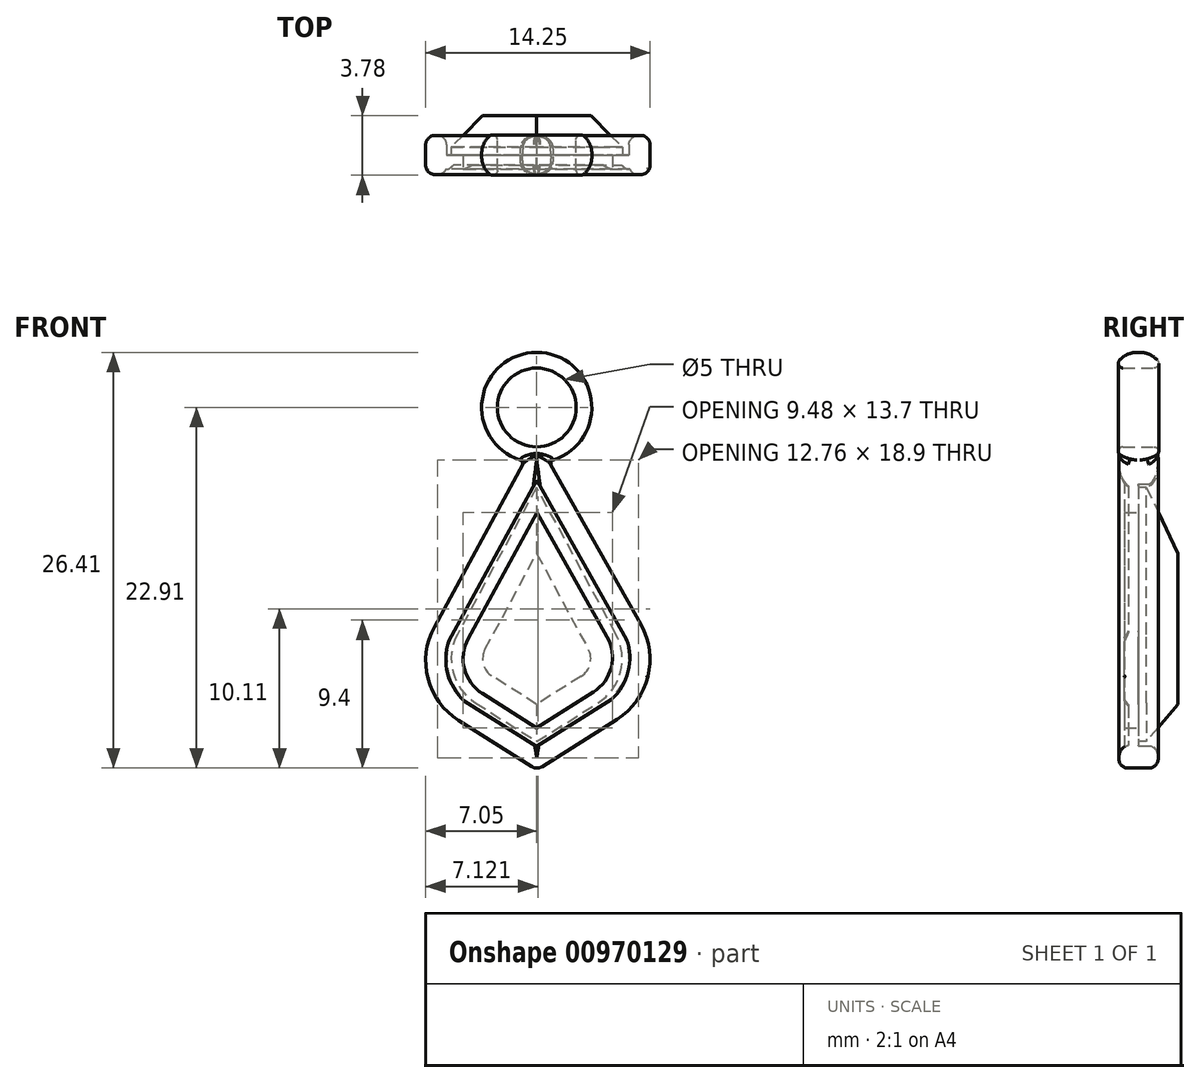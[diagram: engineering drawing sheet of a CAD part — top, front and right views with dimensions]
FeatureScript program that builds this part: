
annotation { "Feature Type Name" : "Feature", "Feature Type Description" : "" }
export const myFeature = defineFeature(function(context is Context, id is Id, definition is map)
    precondition{}
    {
        {
            var Q0;
            Q0=qCreatedBy(makeId("Front.planeOp"),FACE);
            var sketch = newSketch(context, id + "F0", { "sketchPlane" : qUnion([Q0])});
            skCircle(sketch, "E0", {"center": v(0, 12.12) * mm, "radius": 3.5 * mm});
            skCircle(sketch, "E1", {"center": v(0, 12.12) * mm, "radius": 2.5 * mm});
            skSolve(sketch);
        }
        {
            var Q0;
            Q0=makeQuery(id+"F0.imprint","IMPRINT",FACE,{"disambiguationData":[TD([[makeQuery(id+"F0.imprint","IMPRINT",EDGE,{"derivedFrom":sQuery(id+"F0.wireOp",EDGE,"E0")}),1.0]])]});
            extrude(context, id + "F1", {"entities" : qUnion([Q0]), "depth" : 1.5 * mm, "offsetDistance" : 25 * mm, "hasSecondDirection" : true, "secondDirectionOppositeDirection" : true, "secondDirectionDepth" : 1.5 * mm});
        }
        {
            var Q0;
            Q0=makeQuery(id+"F1.opExtrude","CAP_EDGE",EDGE,{"disambiguationData":[OSD([sQuery(id+"F0.wireOp",EDGE,"E0")])],"isStart":true});
            var Q1;
            Q1=makeQuery(id+"F1.opExtrude","CAP_EDGE",EDGE,{"disambiguationData":[OSD([sQuery(id+"F0.wireOp",EDGE,"E0")])],"isStart":false});
            fillet(context, id + "F2", {"entities" : qUnion([Q0, Q1]), "radius" : 1.5 * mm, "tangentPropagation" : true, "allowEdgeOverflow" : false});
        }
        {
            var Q0;
            Q0=makeQuery(id+"F1.opExtrude","SWEPT_FACE",FACE,{"disambiguationData":[OSD([sQuery(id+"F0.wireOp",EDGE,"E1")])]});
            var Q1;
            Q1=makeQuery(id+"F2.opFillet","BLEND_EDGE",EDGE,{"blendedFrom":[makeQuery(id+"F1.opExtrude","CAP_EDGE",EDGE,{"disambiguationData":[OSD([sQuery(id+"F0.wireOp",EDGE,"E0")])],"isStart":true}),makeQuery(id+"F1.opExtrude","SWEPT_FACE",FACE,{"disambiguationData":[OSD([sQuery(id+"F0.wireOp",EDGE,"E1")])]})],"blendedInto":[makeQuery(id+"F1.opExtrude","SWEPT_FACE",FACE,{"disambiguationData":[OSD([sQuery(id+"F0.wireOp",EDGE,"E1")])]})]});
            var Q2;
            Q2=makeQuery(id+"F2.opFillet","BLEND_EDGE",EDGE,{"blendedFrom":[makeQuery(id+"F1.opExtrude","CAP_EDGE",EDGE,{"disambiguationData":[OSD([sQuery(id+"F0.wireOp",EDGE,"E0")])],"isStart":false}),makeQuery(id+"F1.opExtrude","SWEPT_FACE",FACE,{"disambiguationData":[OSD([sQuery(id+"F0.wireOp",EDGE,"E1")])]})],"blendedInto":[makeQuery(id+"F1.opExtrude","SWEPT_FACE",FACE,{"disambiguationData":[OSD([sQuery(id+"F0.wireOp",EDGE,"E1")])]})]});
            fillet(context, id + "F3", {"entities" : qUnion([Q0, Q1, Q2]), "radius" : .3 * mm, "tangentPropagation" : true, "allowEdgeOverflow" : false});
        }
        {
            var Q0;
            Q0=qCreatedBy(makeId("Front.planeOp"),FACE);
            var sketch = newSketch(context, id + "F4", { "sketchPlane" : qUnion([Q0])});
            skLineSegment(sketch, "E2", {"start": v(-0.04, 10.14) * mm, "end": v(8.72, -5.4) * mm});
            skLineSegment(sketch, "E3", {"start": v(8.72, -5.4) * mm, "end": v(0, -10.9) * mm});
            skLineSegment(sketch, "E4.MirrorCS", {"start": v(0, 10.14) * mm, "end": v(-8.52, -5.52) * mm});
            skLineSegment(sketch, "E5.MirrorCS", {"start": v(-8.52, -5.52) * mm, "end": v(0, -10.9) * mm});
            skLineSegment(sketch, "E6.0", {"start": v(0, 7.53) * mm, "end": v(7.04, -4.97) * mm});
            skLineSegment(sketch, "E6.1", {"start": v(0, 7.53) * mm, "end": v(-6.86, -5.09) * mm});
            skLineSegment(sketch, "E6.2", {"start": v(-6.86, -5.09) * mm, "end": v(0, -9.42) * mm});
            skLineSegment(sketch, "E6.3", {"start": v(7.04, -4.97) * mm, "end": v(0, -9.42) * mm});
            skLineSegment(sketch, "E7.0", {"start": v(0.02, 5.46) * mm, "end": v(-5.53, -4.74) * mm});
            skLineSegment(sketch, "E7.1", {"start": v(0.02, 5.46) * mm, "end": v(5.7, -4.63) * mm});
            skLineSegment(sketch, "E7.2", {"start": v(5.7, -4.63) * mm, "end": v(0, -8.24) * mm});
            skLineSegment(sketch, "E7.3", {"start": v(-5.53, -4.74) * mm, "end": v(0, -8.24) * mm});
            skSolve(sketch);
        }
        {
            var Q0;
            Q0=makeQuery(id+"F4.imprint","IMPRINT",FACE,{"disambiguationData":[TD([[makeQuery(id+"F4.imprint","IMPRINT",EDGE,{"derivedFrom":sQuery(id+"F4.wireOp",EDGE,"E2")}),-1.0]])]});
            extrude(context, id + "F5", {"entities" : qUnion([Q0]), "depth" : 1.25 * mm, "offsetDistance" : 25 * mm, "hasSecondDirection" : true, "secondDirectionOppositeDirection" : true, "secondDirectionDepth" : 1.25 * mm});
        }
        {
            var Q0;
            Q0=makeQuery(id+"F5.opExtrude","SWEPT_EDGE",EDGE,{"disambiguationData":[OSD([sQuery(id+"F4.wireOp",EDGE,"E4.MirrorCS"),sQuery(id+"F4.wireOp",EDGE,"E5.MirrorCS")])]});
            var Q1;
            Q1=makeQuery(id+"F5.opExtrude","SWEPT_EDGE",EDGE,{"disambiguationData":[OSD([sQuery(id+"F4.wireOp",EDGE,"E2"),sQuery(id+"F4.wireOp",EDGE,"E3")])]});
            fillet(context, id + "F6", {"entities" : qUnion([Q0, Q1]), "radius" : 4.5 * mm, "tangentPropagation" : true, "allowEdgeOverflow" : false});
        }
        {
            var Q0;
            Q0=makeQuery(id+"F5.opExtrude","SWEPT_EDGE",EDGE,{"disambiguationData":[OSD([sQuery(id+"F4.wireOp",EDGE,"E6.0"),sQuery(id+"F4.wireOp",EDGE,"E6.3")])]});
            var Q1;
            Q1=makeQuery(id+"F5.opExtrude","SWEPT_EDGE",EDGE,{"disambiguationData":[OSD([sQuery(id+"F4.wireOp",EDGE,"E6.1"),sQuery(id+"F4.wireOp",EDGE,"E6.2")])]});
            fillet(context, id + "F7", {"entities" : qUnion([Q0, Q1]), "radius" : 3.5 * mm, "tangentPropagation" : true, "allowEdgeOverflow" : false});
        }
        {
            var Q0;
            {var subQ0=sQuery(id+"F4.wireOp",EDGE,"E3");var subQ1=sQuery(id+"F4.wireOp",EDGE,"E2");Q0=makeQuery(id+"F6.opFillet","BLEND_EDGE",EDGE,{"blendedFrom":[makeQuery(id+"F5.opExtrude","SWEPT_EDGE",EDGE,{"disambiguationData":[OSD([subQ1,subQ0])]}),makeQuery(id+"F5.opExtrude","CAP_FACE",FACE,{"disambiguationData":[OSD([subQ1,subQ0,sQuery(id+"F4.wireOp",EDGE,"E4.MirrorCS"),sQuery(id+"F4.wireOp",EDGE,"E5.MirrorCS"),sQuery(id+"F4.wireOp",EDGE,"E6.0"),sQuery(id+"F4.wireOp",EDGE,"E6.1"),sQuery(id+"F4.wireOp",EDGE,"E6.2"),sQuery(id+"F4.wireOp",EDGE,"E6.3")])],"isStart":false})],"blendedInto":[makeQuery(id+"F5.opExtrude","CAP_FACE",FACE,{"disambiguationData":[OSD([subQ1,subQ0,sQuery(id+"F4.wireOp",EDGE,"E4.MirrorCS"),sQuery(id+"F4.wireOp",EDGE,"E5.MirrorCS"),sQuery(id+"F4.wireOp",EDGE,"E6.0"),sQuery(id+"F4.wireOp",EDGE,"E6.1"),sQuery(id+"F4.wireOp",EDGE,"E6.2"),sQuery(id+"F4.wireOp",EDGE,"E6.3")])],"isStart":false})]});}
            var Q1;
            Q1=makeQuery(id+"F5.opExtrude","CAP_EDGE",EDGE,{"disambiguationData":[OSD([sQuery(id+"F4.wireOp",EDGE,"E3")])],"isStart":false});
            var Q2;
            Q2=makeQuery(id+"F5.opExtrude","CAP_EDGE",EDGE,{"disambiguationData":[OSD([sQuery(id+"F4.wireOp",EDGE,"E6.0")])],"isStart":false});
            var Q3;
            Q3=makeQuery(id+"F5.opExtrude","CAP_EDGE",EDGE,{"disambiguationData":[OSD([sQuery(id+"F4.wireOp",EDGE,"E5.MirrorCS")])],"isStart":false});
            var Q4;
            Q4=makeQuery(id+"F5.opExtrude","CAP_EDGE",EDGE,{"disambiguationData":[OSD([sQuery(id+"F4.wireOp",EDGE,"E6.2")])],"isStart":false});
            var Q5;
            {var subQ0=sQuery(id+"F4.wireOp",EDGE,"E5.MirrorCS");var subQ1=sQuery(id+"F4.wireOp",EDGE,"E4.MirrorCS");Q5=makeQuery(id+"F6.opFillet","BLEND_EDGE",EDGE,{"blendedFrom":[makeQuery(id+"F5.opExtrude","SWEPT_EDGE",EDGE,{"disambiguationData":[OSD([subQ1,subQ0])]}),makeQuery(id+"F5.opExtrude","CAP_FACE",FACE,{"disambiguationData":[OSD([sQuery(id+"F4.wireOp",EDGE,"E2"),sQuery(id+"F4.wireOp",EDGE,"E3"),subQ1,subQ0,sQuery(id+"F4.wireOp",EDGE,"E6.0"),sQuery(id+"F4.wireOp",EDGE,"E6.1"),sQuery(id+"F4.wireOp",EDGE,"E6.2"),sQuery(id+"F4.wireOp",EDGE,"E6.3")])],"isStart":true})],"blendedInto":[makeQuery(id+"F5.opExtrude","CAP_FACE",FACE,{"disambiguationData":[OSD([sQuery(id+"F4.wireOp",EDGE,"E2"),sQuery(id+"F4.wireOp",EDGE,"E3"),subQ1,subQ0,sQuery(id+"F4.wireOp",EDGE,"E6.0"),sQuery(id+"F4.wireOp",EDGE,"E6.1"),sQuery(id+"F4.wireOp",EDGE,"E6.2"),sQuery(id+"F4.wireOp",EDGE,"E6.3")])],"isStart":true})]});}
            var Q6;
            Q6=makeQuery(id+"F5.opExtrude","CAP_EDGE",EDGE,{"disambiguationData":[OSD([sQuery(id+"F4.wireOp",EDGE,"E6.1")])],"isStart":true});
            var Q7;
            Q7=makeQuery(id+"F5.opExtrude","CAP_EDGE",EDGE,{"disambiguationData":[OSD([sQuery(id+"F4.wireOp",EDGE,"E6.0")])],"isStart":true});
            var Q8;
            Q8=makeQuery(id+"F5.opExtrude","CAP_EDGE",EDGE,{"disambiguationData":[OSD([sQuery(id+"F4.wireOp",EDGE,"E3")])],"isStart":true});
            var Q9;
            Q9=makeQuery(id+"F5.opExtrude","SWEPT_EDGE",EDGE,{"disambiguationData":[OSD([sQuery(id+"F4.wireOp",EDGE,"E3"),sQuery(id+"F4.wireOp",EDGE,"E5.MirrorCS")])]});
            fillet(context, id + "F8", {"entities" : qUnion([Q0, Q1, Q2, Q3, Q4, Q5, Q6, Q7, Q8, Q9]), "radius" : .6 * mm, "tangentPropagation" : true, "allowEdgeOverflow" : false});
        }
        {
            var Q0;
            Q0=makeQuery(id+"F8.opFillet","BLEND_EDGE",EDGE,{"blendedFrom":[makeQuery(id+"F5.opExtrude","CAP_EDGE",EDGE,{"disambiguationData":[OSD([sQuery(id+"F4.wireOp",EDGE,"E6.0")])],"isStart":false}),makeQuery(id+"F5.opExtrude","CAP_EDGE",EDGE,{"disambiguationData":[OSD([sQuery(id+"F4.wireOp",EDGE,"E6.1")])],"isStart":false})],"blendedInto":[]});
            var Q1;
            Q1=makeQuery(id+"F5.opExtrude","SWEPT_EDGE",EDGE,{"disambiguationData":[OSD([sQuery(id+"F4.wireOp",EDGE,"E6.2"),sQuery(id+"F4.wireOp",EDGE,"E6.3")])]});
            fillet(context, id + "F9", {"entities" : qUnion([Q0, Q1]), "radius" : .25 * mm, "tangentPropagation" : true, "allowEdgeOverflow" : false});
        }
        {
            var Q0;
            Q0=makeQuery(id+"F5.opExtrude","SWEPT_EDGE",EDGE,{"disambiguationData":[OSD([sQuery(id+"F4.wireOp",EDGE,"E2"),sQuery(id+"F4.wireOp",EDGE,"E4.MirrorCS")])]});
            fillet(context, id + "F10", {"entities" : qUnion([Q0]), "radius" : .5 * mm, "tangentPropagation" : true, "allowEdgeOverflow" : false});
        }
        {
            var Q0;
            Q0=makeQuery(id+"F4.imprint","IMPRINT",FACE,{"disambiguationData":[TD([[makeQuery(id+"F4.imprint","IMPRINT",EDGE,{"derivedFrom":sQuery(id+"F4.wireOp",EDGE,"E6.0")}),-1.0]])]});
            extrude(context, id + "F11", {"entities" : qUnion([Q0]), "depth" : .9 * mm, "offsetDistance" : 25 * mm});
        }
        {
            var Q0;
            Q0=qCreatedBy(makeId("Front.planeOp"),FACE);
            var sketch = newSketch(context, id + "F12", { "sketchPlane" : qUnion([Q0])});
            skLineSegment(sketch, "E8", {"start": v(0, 7.05) * mm, "end": v(-6.5, -5) * mm});
            skLineSegment(sketch, "E9", {"start": v(-6.5, -5) * mm, "end": v(0, -9.1) * mm});
            skLineSegment(sketch, "E10.MirrorCS", {"start": v(6.5, -5) * mm, "end": v(0, -9.1) * mm});
            skLineSegment(sketch, "E11.MirrorCS", {"start": v(0, 7.05) * mm, "end": v(6.5, -5) * mm});
            skSolve(sketch);
        }
        {
            var Q0;
            Q0=qSketchRegion(id+"F12",true);
            extrude(context, id + "F13", {"entities" : qUnion([Q0]), "oppositeDirection" : true, "depth" : 2.5 * mm, "offsetDistance" : 25 * mm});
        }
        {
            var Q0;
            Q0=makeQuery(id+"F13.opExtrude","SWEPT_EDGE",EDGE,{"disambiguationData":[OSD([sQuery(id+"F12.wireOp",EDGE,"E8"),sQuery(id+"F12.wireOp",EDGE,"E9")])]});
            var Q1;
            Q1=makeQuery(id+"F13.opExtrude","SWEPT_EDGE",EDGE,{"disambiguationData":[OSD([sQuery(id+"F12.wireOp",EDGE,"E10.MirrorCS"),sQuery(id+"F12.wireOp",EDGE,"E11.MirrorCS")])]});
            fillet(context, id + "F14", {"entities" : qUnion([Q0, Q1]), "radius" : 3.3 * mm, "tangentPropagation" : true, "allowEdgeOverflow" : false});
        }
        {
            var Q0;
            Q0=makeQuery(id+"F11.opExtrude","SWEPT_BODY",BODY,{"disambiguationData":[OSD([sQuery(id+"F4.wireOp",EDGE,"E6.0"),sQuery(id+"F4.wireOp",EDGE,"E6.1"),sQuery(id+"F4.wireOp",EDGE,"E6.2"),sQuery(id+"F4.wireOp",EDGE,"E6.3")])]});
            var Q1;
            Q1=makeQuery(id+"F1.opExtrude","SWEPT_BODY",BODY,{"disambiguationData":[OSD([sQuery(id+"F0.wireOp",EDGE,"E0"),sQuery(id+"F0.wireOp",EDGE,"E1")])]});
            var Q2;
            Q2=makeQuery(id+"F5.opExtrude","SWEPT_BODY",BODY,{"disambiguationData":[OSD([sQuery(id+"F4.wireOp",EDGE,"E2"),sQuery(id+"F4.wireOp",EDGE,"E3"),sQuery(id+"F4.wireOp",EDGE,"E4.MirrorCS"),sQuery(id+"F4.wireOp",EDGE,"E5.MirrorCS"),sQuery(id+"F4.wireOp",EDGE,"E6.0"),sQuery(id+"F4.wireOp",EDGE,"E6.1"),sQuery(id+"F4.wireOp",EDGE,"E6.2"),sQuery(id+"F4.wireOp",EDGE,"E6.3")])]});
            booleanBodies(context, id + "F15", {"operationType" : BooleanOperationType.UNION, "tools" : qUnion([Q0, Q1, Q2])});
        }
        {
            var Q0;
            {var subQ0=sQuery(id+"F0.wireOp",EDGE,"E0");Q0=makeQuery(id+"F15.opBoolean","INTERSECT",EDGE,{"derivedFrom":[makeQuery(id+"F2.opFillet","BLEND_FACE",FACE,{"disambiguationData":[OSD([subQ0]),TDD([makeQuery(id+"F1.opExtrude","CAP_EDGE",EDGE,{"disambiguationData":[OSD([subQ0])],"isStart":false})])]}),makeQuery(id+"F5.opExtrude","SWEPT_FACE",FACE,{"disambiguationData":[OSD([sQuery(id+"F4.wireOp",EDGE,"E2")])]})]});}
            fillet(context, id + "F16", {"entities" : qUnion([Q0]), "radius" : .25 * mm, "tangentPropagation" : true, "allowEdgeOverflow" : false});
        }
        {
            var Q0;
            Q0=makeQuery(id+"F11.opExtrude","SWEPT_EDGE",EDGE,{"disambiguationData":[OSD([sQuery(id+"F4.wireOp",EDGE,"E7.0"),sQuery(id+"F4.wireOp",EDGE,"E7.3")])]});
            var Q1;
            Q1=makeQuery(id+"F11.opExtrude","SWEPT_EDGE",EDGE,{"disambiguationData":[OSD([sQuery(id+"F4.wireOp",EDGE,"E7.1"),sQuery(id+"F4.wireOp",EDGE,"E7.2")])]});
            fillet(context, id + "F17", {"entities" : qUnion([Q0, Q1]), "radius" : 2.63 * mm, "tangentPropagation" : true, "allowEdgeOverflow" : false});
        }
        {
            var Q0;
            Q0=makeQuery(id+"F13.opExtrude","CAP_FACE",FACE,{"disambiguationData":[OSD([sQuery(id+"F12.wireOp",EDGE,"E8"),sQuery(id+"F12.wireOp",EDGE,"E9"),sQuery(id+"F12.wireOp",EDGE,"E10.MirrorCS"),sQuery(id+"F12.wireOp",EDGE,"E11.MirrorCS")])],"isStart":false});
            chamfer(context, id + "F18", {"entities" : qUnion([Q0]), "width" : 2 * mm, "tangentPropagation" : true});
        }
    });
